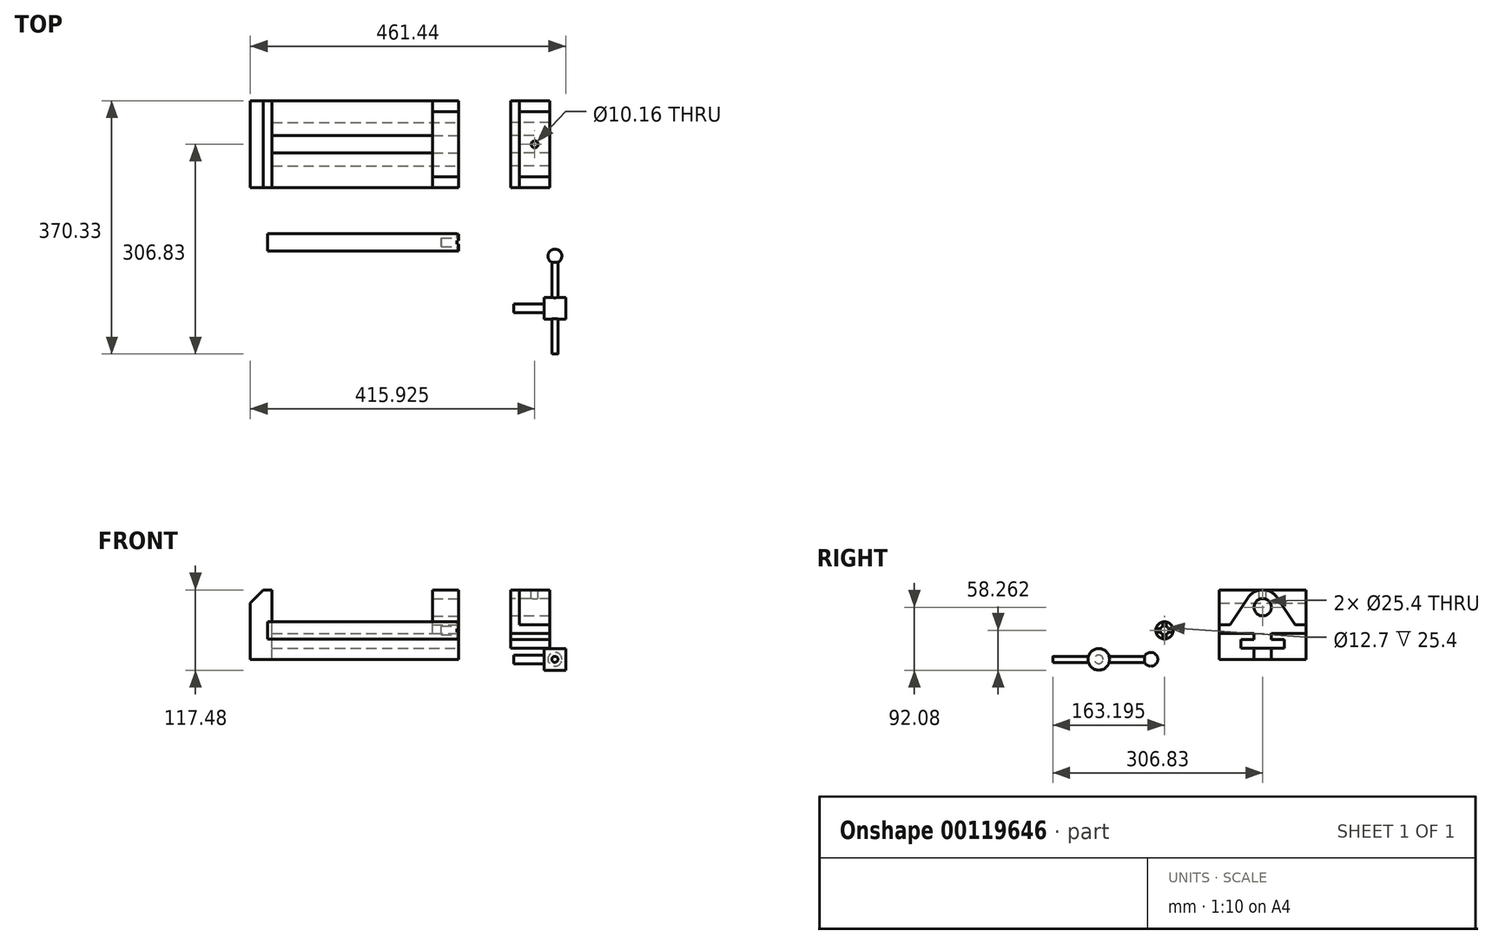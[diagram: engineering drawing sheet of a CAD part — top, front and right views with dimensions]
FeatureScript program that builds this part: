
annotation { "Feature Type Name" : "Feature", "Feature Type Description" : "" }
export const myFeature = defineFeature(function(context is Context, id is Id, definition is map)
    precondition{}
    {
        {
            var Q0;
            Q0=qCreatedBy(makeId("Right.planeOp"),FACE);
            var sketch = newSketch(context, id + "F0", { "sketchPlane" : qUnion([Q0])});
            skLineSegment(sketch, "E0", {"start": v(0, 0) * mm, "end": v(127, 0) * mm});
            skLineSegment(sketch, "E1", {"start": v(127, 0) * mm, "end": v(127, 50.8) * mm});
            skLineSegment(sketch, "E2", {"start": v(127, 50.8) * mm, "end": v(111.12, 50.8) * mm});
            skLineSegment(sketch, "E3", {"start": v(111.12, 50.8) * mm, "end": v(84.6, 90.35) * mm});
            skLineSegment(sketch, "E4", {"start": v(0, 0) * mm, "end": v(0, 50.8) * mm});
            skLineSegment(sketch, "E5", {"start": v(0, 50.8) * mm, "end": v(15.88, 50.8) * mm});
            skLineSegment(sketch, "E6", {"start": v(15.88, 50.8) * mm, "end": v(42.4, 90.35) * mm});
            skLineSegment(sketch, "E7", {"start": v(50.8, 0) * mm, "end": v(50.8, 16.51) * mm});
            skLineSegment(sketch, "E8", {"start": v(50.8, 16.51) * mm, "end": v(31.75, 16.5) * mm});
            skLineSegment(sketch, "E9", {"start": v(31.75, 16.51) * mm, "end": v(31.75, 29.2) * mm});
            skLineSegment(sketch, "E10", {"start": v(31.75, 29.2) * mm, "end": v(50.8, 29.2) * mm});
            skLineSegment(sketch, "E11", {"start": v(50.8, 29.2) * mm, "end": v(50.8, 38.1) * mm});
            skLineSegment(sketch, "E12", {"start": v(50.8, 38.1) * mm, "end": v(76.2, 38.1) * mm});
            skLineSegment(sketch, "E13", {"start": v(76.2, 38.1) * mm, "end": v(76.2, 29.2) * mm});
            skLineSegment(sketch, "E14", {"start": v(76.2, 29.2) * mm, "end": v(95.25, 29.2) * mm});
            skLineSegment(sketch, "E15", {"start": v(95.25, 29.2) * mm, "end": v(95.25, 16.51) * mm});
            skLineSegment(sketch, "E16", {"start": v(95.25, 16.51) * mm, "end": v(76.2, 16.51) * mm});
            skLineSegment(sketch, "E17", {"start": v(76.2, 16.51) * mm, "end": v(76.2, 0) * mm});
            skLineSegment(sketch, "E18", {"start": v(63.5, 0) * mm, "end": v(63.5, 76.2) * mm, "construction": true});
            skCircle(sketch, "E19", {"center": v(63.5, 76.2) * mm, "radius": 12.7 * mm});
            skArc(sketch, "E20", {"start": v(84.6, 90.35) * mm, "mid": v(63.5, 101.6) * mm, "end": v(42.4, 90.35) * mm});
            skLineSegment(sketch, "E21", {"start": v(15.88, 50.8) * mm, "end": v(111.12, 50.8) * mm});
            skLineSegment(sketch, "E22", {"start": v(50.8, 38.1) * mm, "end": v(0, 38.1) * mm});
            skLineSegment(sketch, "E23", {"start": v(76.2, 38.1) * mm, "end": v(127, 38.1) * mm});
            skSolve(sketch);
        }
        {
            var Q0;
            {var subQ0=sQuery(id+"F0.wireOp",EDGE,"E7");Q0=makeQuery(id+"F0.imprint","IMPRINT",FACE,{"disambiguationData":[TD([[makeQuery(id+"F0.imprint","IMPRINT",EDGE,{"derivedFrom":subQ0}),1.0]])]});}
            var Q1;
            Q1=makeQuery(id+"F0.imprint","IMPRINT",FACE,{"disambiguationData":[TD([[makeQuery(id+"F0.imprint","IMPRINT",EDGE,{"derivedFrom":sQuery(id+"F0.wireOp",EDGE,"E13")}),1.0]])]});
            var Q2;
            Q2=makeQuery(id+"F0.imprint","IMPRINT",FACE,{"disambiguationData":[TD([[makeQuery(id+"F0.imprint","IMPRINT",EDGE,{"derivedFrom":sQuery(id+"F0.wireOp",EDGE,"E3")}),1.0]])]});
            var Q3;
            {var subQ3=sQuery(id+"F0.wireOp",EDGE,"E2");Q3=makeQuery(id+"F0.imprint","IMPRINT",FACE,{"disambiguationData":[TD([[makeQuery(id+"F0.imprint","IMPRINT",EDGE,{"derivedFrom":subQ3}),1.0]])]});}
            extrude(context, id + "F1", {"entities" : qUnion([Q0, Q1, Q2, Q3]), "oppositeDirection" : true, "depth" : 38.1 * mm});
        }
        {
            var Q0;
            Q0=makeQuery(id+"F0.imprint","IMPRINT",FACE,{"disambiguationData":[TD([[makeQuery(id+"F0.imprint","IMPRINT",EDGE,{"derivedFrom":sQuery(id+"F0.wireOp",EDGE,"E13")}),1.0]])]});
            var Q1;
            {var subQ0=sQuery(id+"F0.wireOp",EDGE,"E7");Q1=makeQuery(id+"F0.imprint","IMPRINT",FACE,{"disambiguationData":[TD([[makeQuery(id+"F0.imprint","IMPRINT",EDGE,{"derivedFrom":subQ0}),1.0]])]});}
            extrude(context, id + "F2", {"entities" : qUnion([Q0, Q1]), "operationType" : NewBodyOperationType.ADD, "oppositeDirection" : true, "depth" : 304.8 * mm});
        }
        {
            var Q0;
            Q0=makeQuery(id+"F2.opExtrude","CAP_FACE",FACE,{"disambiguationData":[OSD([sQuery(id+"F0.wireOp",EDGE,"E0"),sQuery(id+"F0.wireOp",EDGE,"E4"),sQuery(id+"F0.wireOp",EDGE,"E7"),sQuery(id+"F0.wireOp",EDGE,"E8"),sQuery(id+"F0.wireOp",EDGE,"E9"),sQuery(id+"F0.wireOp",EDGE,"E10"),sQuery(id+"F0.wireOp",EDGE,"E11"),sQuery(id+"F0.wireOp",EDGE,"E22")])],"isStart":false});
            var sketch = newSketch(context, id + "F3", { "sketchPlane" : qUnion([Q0])});
            skLineSegment(sketch, "E24.bottom", {"start": v(0, 0) * mm, "end": v(-127, 0) * mm});
            skLineSegment(sketch, "E24.top", {"start": v(0, 101.6) * mm, "end": v(-127, 101.6) * mm});
            skLineSegment(sketch, "E24.left", {"start": v(0, 0) * mm, "end": v(0, 101.6) * mm});
            skLineSegment(sketch, "E24.right", {"start": v(-127, 0) * mm, "end": v(-127, 101.6) * mm});
            skSolve(sketch);
        }
        {
            var Q0;
            Q0 = qSketchRegion(id + "F3", true);
            extrude(context, id + "F4", {"entities" : qUnion([Q0]), "operationType" : NewBodyOperationType.ADD, "oppositeDirection" : true, "depth" : 31.75 * mm});
        }
        {
            var Q0;
            Q0=makeQuery(id+"F4.opExtrude","CAP_EDGE",EDGE,{"disambiguationData":[OSD([sQuery(id+"F3.wireOp",EDGE,"E24.top")])],"isStart":true});
            chamfer(context, id + "F5", {"entities" : qUnion([Q0]), "chamferType" : ChamferType.TWO_OFFSETS, "width1" : 19.05 * mm, "oppositeDirection" : false, "width2" : 19.05 * mm, "tangentPropagation" : true});
        }
        {
            var Q0;
            {var subQ0=sQuery(id+"F0.wireOp",EDGE,"E7");Q0=makeQuery(id+"F0.imprint","IMPRINT",FACE,{"disambiguationData":[TD([[makeQuery(id+"F0.imprint","IMPRINT",EDGE,{"derivedFrom":subQ0}),1.0]])]});}
            cPlane(context, id + "F6", {"entities" : qUnion([Q0]), "cplaneType" : CPlaneType.OFFSET, "offset" : 76.2 * mm, "width" : 152.4 * mm, "height" : 152.4 * mm});
        }
        {
            var Q0;
            Q0=qCreatedBy(id+"F6.planeOp",FACE);
            var sketch = newSketch(context, id + "F7", { "sketchPlane" : qUnion([Q0])});
            skLineSegment(sketch, "E25.0.0", {"start": v(15.88, 50.8) * mm, "end": v(111.12, 50.8) * mm});
            skLineSegment(sketch, "E25.0.1", {"start": v(111.12, 50.8) * mm, "end": v(84.6, 90.35) * mm});
            skArc(sketch, "E25.0.2", {"start": v(84.6, 90.35) * mm, "mid": v(63.5, 101.6) * mm, "end": v(42.4, 90.35) * mm});
            skLineSegment(sketch, "E25.0.3", {"start": v(42.4, 90.35) * mm, "end": v(15.88, 50.8) * mm});
            skLineSegment(sketch, "E26.0.0", {"start": v(76.2, 38.1) * mm, "end": v(127, 38.1) * mm});
            skLineSegment(sketch, "E26.0.1", {"start": v(127, 38.1) * mm, "end": v(127, 50.8) * mm});
            skLineSegment(sketch, "E26.0.2", {"start": v(127, 50.8) * mm, "end": v(111.12, 50.8) * mm});
            skLineSegment(sketch, "E26.0.3", {"start": v(111.12, 50.8) * mm, "end": v(15.88, 50.8) * mm});
            skLineSegment(sketch, "E26.0.4", {"start": v(15.88, 50.8) * mm, "end": v(0, 50.8) * mm});
            skLineSegment(sketch, "E26.0.5", {"start": v(0, 50.8) * mm, "end": v(0, 38.1) * mm});
            skLineSegment(sketch, "E26.0.6", {"start": v(0, 38.1) * mm, "end": v(50.8, 38.1) * mm});
            skLineSegment(sketch, "E26.0.7", {"start": v(50.8, 38.1) * mm, "end": v(76.2, 38.1) * mm});
            skLineSegment(sketch, "E27.0.0", {"start": v(76.2, 16.51) * mm, "end": v(76.2, 0) * mm});
            skLineSegment(sketch, "E27.0.1", {"start": v(76.2, 0) * mm, "end": v(127, 0) * mm});
            skLineSegment(sketch, "E27.0.2", {"start": v(127, 0) * mm, "end": v(127, 38.1) * mm});
            skLineSegment(sketch, "E27.0.3", {"start": v(127, 38.1) * mm, "end": v(76.2, 38.1) * mm});
            skLineSegment(sketch, "E27.0.4", {"start": v(76.2, 38.1) * mm, "end": v(76.2, 29.2) * mm});
            skLineSegment(sketch, "E27.0.5", {"start": v(76.2, 29.2) * mm, "end": v(95.25, 29.2) * mm});
            skLineSegment(sketch, "E27.0.6", {"start": v(95.25, 29.2) * mm, "end": v(95.25, 16.51) * mm});
            skLineSegment(sketch, "E27.0.7", {"start": v(95.25, 16.51) * mm, "end": v(76.2, 16.51) * mm});
            skLineSegment(sketch, "E28.0.0", {"start": v(0, 38.1) * mm, "end": v(0, 0) * mm});
            skLineSegment(sketch, "E28.0.1", {"start": v(0, 0) * mm, "end": v(50.8, 0) * mm});
            skLineSegment(sketch, "E28.0.2", {"start": v(50.8, 0) * mm, "end": v(50.8, 16.51) * mm});
            skLineSegment(sketch, "E28.0.3", {"start": v(50.8, 16.51) * mm, "end": v(31.75, 16.5) * mm});
            skLineSegment(sketch, "E28.0.4", {"start": v(31.75, 16.51) * mm, "end": v(31.75, 29.2) * mm});
            skLineSegment(sketch, "E28.0.5", {"start": v(31.75, 29.2) * mm, "end": v(50.8, 29.2) * mm});
            skLineSegment(sketch, "E28.0.6", {"start": v(50.8, 29.2) * mm, "end": v(50.8, 38.1) * mm});
            skLineSegment(sketch, "E28.0.7", {"start": v(50.8, 38.1) * mm, "end": v(0, 38.1) * mm});
            skLineSegment(sketch, "E29.0", {"start": v(0, 0) * mm, "end": v(127, 0) * mm});
            skLineSegment(sketch, "E30", {"start": v(76.2, 16.51) * mm, "end": v(50.8, 16.51) * mm});
            skLineSegment(sketch, "E31.0.0", {"start": v(50.8, 16.51) * mm, "end": v(50.8, 0) * mm});
            skLineSegment(sketch, "E31.0.1", {"start": v(50.8, 0) * mm, "end": v(76.2, 0) * mm});
            skLineSegment(sketch, "E31.0.2", {"start": v(76.2, 0) * mm, "end": v(76.2, 16.51) * mm});
            skLineSegment(sketch, "E31.0.3", {"start": v(76.2, 16.51) * mm, "end": v(95.25, 16.51) * mm});
            skLineSegment(sketch, "E31.0.4", {"start": v(95.25, 16.51) * mm, "end": v(95.25, 29.2) * mm});
            skLineSegment(sketch, "E31.0.5", {"start": v(95.25, 29.2) * mm, "end": v(76.2, 29.2) * mm});
            skLineSegment(sketch, "E31.0.6", {"start": v(76.2, 29.2) * mm, "end": v(76.2, 38.1) * mm});
            skLineSegment(sketch, "E31.0.8", {"start": v(127, 38.1) * mm, "end": v(127, 101.6) * mm});
            skLineSegment(sketch, "E31.0.9", {"start": v(127, 101.6) * mm, "end": v(0, 101.6) * mm});
            skLineSegment(sketch, "E31.0.10", {"start": v(0, 101.6) * mm, "end": v(0, 38.1) * mm});
            skLineSegment(sketch, "E31.0.12", {"start": v(50.8, 38.1) * mm, "end": v(50.8, 29.2) * mm});
            skLineSegment(sketch, "E31.0.13", {"start": v(50.8, 29.2) * mm, "end": v(31.75, 29.2) * mm});
            skLineSegment(sketch, "E31.0.14", {"start": v(31.75, 29.2) * mm, "end": v(31.75, 16.51) * mm});
            skLineSegment(sketch, "E31.0.15", {"start": v(31.75, 16.5) * mm, "end": v(50.8, 16.51) * mm});
            skCircle(sketch, "E32.0", {"center": v(63.5, 76.2) * mm, "radius": 12.7 * mm});
            skSolve(sketch);
        }
        {
            var Q0;
            {var subQ2=sQuery(id+"F7.wireOp",EDGE,"E26.0.2");Q0=makeQuery(id+"F7.imprint","IMPRINT",FACE,{"disambiguationData":[TD([[makeQuery(id+"F7.imprint","IMPRINT",EDGE,{"derivedFrom":subQ2}),1.0]])]});}
            var Q1;
            {var subQ3=sQuery(id+"F7.wireOp",EDGE,"E25.0.1");Q1=makeQuery(id+"F7.imprint","IMPRINT",FACE,{"disambiguationData":[TD([[makeQuery(id+"F7.imprint","IMPRINT",EDGE,{"derivedFrom":subQ3}),1.0]])]});}
            var Q2;
            Q2=makeQuery(id+"F7.imprint","IMPRINT",FACE,{"disambiguationData":[TD([[makeQuery(id+"F7.imprint","IMPRINT",EDGE,{"derivedFrom":sQuery(id+"F7.wireOp",EDGE,"E26.0.7")}),-1.0]])]});
            extrude(context, id + "F8", {"entities" : qUnion([Q0, Q1, Q2]), "depth" : 57.15 * mm});
        }
        {
            var Q0;
            {var subQ5=sQuery(id+"F7.wireOp",EDGE,"E25.0.3");Q0=makeQuery(id+"F7.imprint","IMPRINT",FACE,{"disambiguationData":[TD([[makeQuery(id+"F7.imprint","IMPRINT",EDGE,{"derivedFrom":subQ5}),-1.0]])]});}
            var Q1;
            {var subQ5=sQuery(id+"F7.wireOp",EDGE,"E25.0.1");Q1=makeQuery(id+"F7.imprint","IMPRINT",FACE,{"disambiguationData":[TD([[makeQuery(id+"F7.imprint","IMPRINT",EDGE,{"derivedFrom":subQ5}),-1.0]])]});}
            extrude(context, id + "F9", {"entities" : qUnion([Q0, Q1]), "operationType" : NewBodyOperationType.ADD, "depth" : 12.7 * mm});
        }
        {
            var Q0;
            {var subQ0=sQuery(id+"F7.wireOp",EDGE,"E31.0.9");Q0=makeQuery(id+"F9.boolean.opBoolean","MERGE",FACE,{"derivedFrom":[makeQuery(id+"F9.opExtrude","SWEPT_FACE",FACE,{"disambiguationData":[OSD([subQ0]),TDD([makeQuery(id+"F7.imprint","IMPRINT",EDGE,{"disambiguationData":[TD([[makeQuery(id+"F7.imprint","INTERSECT",VERTEX,{"derivedFrom":[sQuery(id+"F7.wireOp",EDGE,"E31.0.8"),subQ0]}),-1.0]])],"derivedFrom":subQ0})])]}),makeQuery(id+"F9.opExtrude","SWEPT_FACE",FACE,{"disambiguationData":[OSD([subQ0]),TDD([makeQuery(id+"F7.imprint","IMPRINT",EDGE,{"disambiguationData":[TD([[makeQuery(id+"F7.imprint","INTERSECT",VERTEX,{"derivedFrom":[subQ0,sQuery(id+"F7.wireOp",EDGE,"E31.0.10")]}),1.0]])],"derivedFrom":subQ0})])]})]});}
            var sketch = newSketch(context, id + "F10", { "sketchPlane" : qUnion([Q0])});
            skCircle(sketch, "E33", {"center": v(111.13, 63.5) * mm, "radius": 5.08 * mm});
            skSolve(sketch);
        }
        {
            var Q0;
            Q0=makeQuery(id+"F10.imprint","IMPRINT",FACE,{"disambiguationData":[TD([[makeQuery(id+"F10.imprint","IMPRINT",EDGE,{"derivedFrom":sQuery(id+"F10.wireOp",EDGE,"E33")}),1.0]])]});
            var Q1;
            Q1=makeQuery(id+"F8.opExtrude","SWEPT_FACE",FACE,{"disambiguationData":[OSD([sQuery(id+"F7.wireOp",EDGE,"E32.0")])]});
            extrude(context, id + "F11", {"entities" : qUnion([Q0]), "operationType" : NewBodyOperationType.REMOVE, "endBound" : BoundingType.UP_TO_SURFACE, "oppositeDirection" : true, "endBoundEntityFace" : qUnion([Q1]), "depth" : 25.4 * mm});
        }
        {
            var Q0;
            Q0=qCreatedBy(makeId("Right.planeOp"),FACE);
            var sketch = newSketch(context, id + "F12", { "sketchPlane" : qUnion([Q0])});
            skCircle(sketch, "E34", {"center": v(-80.14, 42.38) * mm, "radius": 6.35 * mm});
            skCircle(sketch, "E35", {"center": v(-80.14, 42.38) * mm, "radius": 12.7 * mm});
            skLineSegment(sketch, "E36", {"start": v(-80.14, 42.38) * mm, "end": v(0, 0) * mm, "construction": true});
            skLineSegment(sketch, "E37", {"start": v(-82.68, 36.56) * mm, "end": v(-82.68, 29.94) * mm});
            skLineSegment(sketch, "E38", {"start": v(-77.6, 36.56) * mm, "end": v(-77.6, 29.94) * mm});
            skLineSegment(sketch, "E39", {"start": v(-82.68, 48.2) * mm, "end": v(-82.68, 54.83) * mm});
            skLineSegment(sketch, "E40", {"start": v(-77.6, 48.2) * mm, "end": v(-77.6, 54.83) * mm});
            skLineSegment(sketch, "E41", {"start": v(-74.32, 44.92) * mm, "end": v(-67.7, 44.92) * mm});
            skLineSegment(sketch, "E42", {"start": v(-74.32, 39.84) * mm, "end": v(-67.7, 39.84) * mm});
            skLineSegment(sketch, "E43", {"start": v(-85.96, 44.92) * mm, "end": v(-92.58, 44.92) * mm});
            skLineSegment(sketch, "E44", {"start": v(-85.96, 39.84) * mm, "end": v(-92.58, 39.84) * mm});
            skSolve(sketch);
        }
        {
            var Q0;
            Q0 = qSketchRegion(id + "F12", true);
            var Q1;
            {var subQ0=sQuery(id+"F12.wireOp",EDGE,"E34");var subQ6=makeQuery(id+"F12.imprint","INTERSECT",VERTEX,{"derivedFrom":[subQ0,sQuery(id+"F12.wireOp",EDGE,"E40")]});Q1=makeQuery(id+"F12.imprint","IMPRINT",FACE,{"disambiguationData":[TD([[makeQuery(id+"F12.imprint","IMPRINT",EDGE,{"disambiguationData":[TD([[subQ6,1.0]])],"derivedFrom":subQ0}),1.0]])]});}
            extrude(context, id + "F13", {"entities" : qUnion([Q0, Q1]), "oppositeDirection" : true, "depth" : 279.4 * mm});
        }
        {
            var Q0;
            {var subQ0=sQuery(id+"F12.wireOp",EDGE,"E34");var subQ6=makeQuery(id+"F12.imprint","INTERSECT",VERTEX,{"derivedFrom":[subQ0,sQuery(id+"F12.wireOp",EDGE,"E40")]});Q0=makeQuery(id+"F12.imprint","IMPRINT",FACE,{"disambiguationData":[TD([[makeQuery(id+"F12.imprint","IMPRINT",EDGE,{"disambiguationData":[TD([[subQ6,1.0]])],"derivedFrom":subQ0}),1.0]])]});}
            extrude(context, id + "F14", {"entities" : qUnion([Q0]), "operationType" : NewBodyOperationType.REMOVE, "oppositeDirection" : true, "depth" : 25.4 * mm});
        }
        {
            var Q0;
            {var subQ0=sQuery(id+"F12.wireOp",EDGE,"E39");Q0=makeQuery(id+"F12.imprint","IMPRINT",FACE,{"disambiguationData":[TD([[makeQuery(id+"F12.imprint","IMPRINT",EDGE,{"derivedFrom":subQ0}),-1.0]])]});}
            var Q1;
            {var subQ0=sQuery(id+"F12.wireOp",EDGE,"E41");Q1=makeQuery(id+"F12.imprint","IMPRINT",FACE,{"disambiguationData":[TD([[makeQuery(id+"F12.imprint","IMPRINT",EDGE,{"derivedFrom":subQ0}),-1.0]])]});}
            var Q2;
            {var subQ0=sQuery(id+"F12.wireOp",EDGE,"E37");Q2=makeQuery(id+"F12.imprint","IMPRINT",FACE,{"disambiguationData":[TD([[makeQuery(id+"F12.imprint","IMPRINT",EDGE,{"derivedFrom":subQ0}),1.0]])]});}
            var Q3;
            {var subQ0=sQuery(id+"F12.wireOp",EDGE,"E43");Q3=makeQuery(id+"F12.imprint","IMPRINT",FACE,{"disambiguationData":[TD([[makeQuery(id+"F12.imprint","IMPRINT",EDGE,{"derivedFrom":subQ0}),1.0]])]});}
            extrude(context, id + "F15", {"entities" : qUnion([Q0, Q1, Q2, Q3]), "operationType" : NewBodyOperationType.REMOVE, "oppositeDirection" : true, "depth" : 2.54 * mm});
        }
        {
            var Q0;
            Q0=qCreatedBy(makeId("Top.planeOp"),FACE);
            var sketch = newSketch(context, id + "F16", { "sketchPlane" : qUnion([Q0])});
            skLineSegment(sketch, "E45", {"start": v(0, 0) * mm, "end": v(140.77, -176.27) * mm, "construction": true});
            skLineSegment(sketch, "E46", {"start": v(140.77, -176.27) * mm, "end": v(140.77, -100.07) * mm, "construction": true});
            skLineSegment(sketch, "E47", {"start": v(171.85, -176.27) * mm, "end": v(140.77, -176.27) * mm, "construction": true});
            skLineSegment(sketch, "E48", {"start": v(54.06, -176.27) * mm, "end": v(140.77, -176.27) * mm, "construction": true});
            skLineSegment(sketch, "E49", {"start": v(145.21, -100.07) * mm, "end": v(145.21, -176.27) * mm});
            skLineSegment(sketch, "E50", {"start": v(136.32, -100.07) * mm, "end": v(136.32, -176.27) * mm});
            skLineSegment(sketch, "E51", {"start": v(145.21, -100.07) * mm, "end": v(136.32, -100.07) * mm});
            skCircle(sketch, "E52", {"center": v(140.77, -100.07) * mm, "radius": 10.16 * mm});
            skLineSegment(sketch, "E53", {"start": v(156.64, -160.4) * mm, "end": v(124.9, -160.4) * mm});
            skLineSegment(sketch, "E54", {"start": v(156.64, -160.4) * mm, "end": v(156.64, -176.27) * mm});
            skLineSegment(sketch, "E55", {"start": v(124.9, -160.4) * mm, "end": v(124.9, -176.27) * mm});
            skLineSegment(sketch, "E56", {"start": v(124.9, -169.92) * mm, "end": v(80.44, -169.92) * mm});
            skLineSegment(sketch, "E57", {"start": v(80.44, -169.92) * mm, "end": v(80.44, -176.27) * mm});
            skLineSegment(sketch, "E58.MirrorCS", {"start": v(156.64, -192.14) * mm, "end": v(156.64, -176.27) * mm});
            skLineSegment(sketch, "E59.MirrorCS", {"start": v(156.64, -192.14) * mm, "end": v(124.9, -192.14) * mm});
            skLineSegment(sketch, "E60.MirrorCS", {"start": v(124.9, -192.14) * mm, "end": v(124.9, -176.27) * mm});
            skLineSegment(sketch, "E61.MirrorCS", {"start": v(124.9, -182.62) * mm, "end": v(80.44, -182.62) * mm});
            skLineSegment(sketch, "E62.MirrorCS", {"start": v(80.44, -182.62) * mm, "end": v(80.44, -176.27) * mm});
            skCircle(sketch, "E63.MirrorC", {"center": v(140.77, -252.47) * mm, "radius": 10.16 * mm});
            skLineSegment(sketch, "E64.MirrorCS", {"start": v(145.21, -252.47) * mm, "end": v(145.21, -176.27) * mm});
            skLineSegment(sketch, "E65.MirrorCS", {"start": v(136.32, -252.47) * mm, "end": v(136.32, -176.27) * mm});
            skLineSegment(sketch, "E66.MirrorCS", {"start": v(145.21, -252.47) * mm, "end": v(136.32, -252.47) * mm});
            skLineSegment(sketch, "E67", {"start": v(140.77, -89.9) * mm, "end": v(140.77, -262.63) * mm});
            skLineSegment(sketch, "E68", {"start": v(156.64, -176.27) * mm, "end": v(80.44, -176.27) * mm});
            skSolve(sketch);
        }
        {
            var Q0;
            {var subQ0=sQuery(id+"F16.wireOp",EDGE,"E51");var subQ1=sQuery(id+"F16.wireOp",EDGE,"E49");var subQ2=makeQuery(id+"F16.imprint","INTERSECT",VERTEX,{"derivedFrom":[subQ1,subQ0]});Q0=makeQuery(id+"F16.imprint","IMPRINT",FACE,{"disambiguationData":[TD([[makeQuery(id+"F16.imprint","IMPRINT",EDGE,{"disambiguationData":[TD([[subQ2,-1.0]])],"derivedFrom":subQ1}),1.0]])]});}
            var Q1;
            {var subQ0=sQuery(id+"F16.wireOp",EDGE,"E51");var subQ1=sQuery(id+"F16.wireOp",EDGE,"E49");var subQ2=makeQuery(id+"F16.imprint","INTERSECT",VERTEX,{"derivedFrom":[subQ1,subQ0]});Q1=makeQuery(id+"F16.imprint","IMPRINT",FACE,{"disambiguationData":[TD([[makeQuery(id+"F16.imprint","IMPRINT",EDGE,{"disambiguationData":[TD([[subQ2,-1.0]])],"derivedFrom":subQ1}),-1.0]])]});}
            var Q2;
            {var subQ0=sQuery(id+"F16.wireOp",EDGE,"E52");var subQ1=sQuery(id+"F16.wireOp",EDGE,"E49");var subQ2=makeQuery(id+"F16.imprint","INTERSECT",VERTEX,{"derivedFrom":[subQ1,subQ0]});Q2=makeQuery(id+"F16.imprint","IMPRINT",FACE,{"disambiguationData":[TD([[makeQuery(id+"F16.imprint","IMPRINT",EDGE,{"disambiguationData":[TD([[subQ2,-1.0]])],"derivedFrom":subQ1}),-1.0]])]});}
            var Q3;
            {var subQ1=sQuery(id+"F16.wireOp",EDGE,"E49");var subQ3=sQuery(id+"F16.wireOp",EDGE,"E53");var subQ4=makeQuery(id+"F16.imprint","INTERSECT",VERTEX,{"derivedFrom":[subQ1,subQ3]});Q3=makeQuery(id+"F16.imprint","IMPRINT",FACE,{"disambiguationData":[TD([[makeQuery(id+"F16.imprint","IMPRINT",EDGE,{"disambiguationData":[TD([[subQ4,-1.0]])],"derivedFrom":subQ3}),1.0]])]});}
            var Q4;
            {var subQ0=sQuery(id+"F16.wireOp",EDGE,"E64.MirrorCS");var subQ1=sQuery(id+"F16.wireOp",EDGE,"E59.MirrorCS");var subQ2=makeQuery(id+"F16.imprint","INTERSECT",VERTEX,{"derivedFrom":[subQ1,subQ0]});Q4=makeQuery(id+"F16.imprint","IMPRINT",FACE,{"disambiguationData":[TD([[makeQuery(id+"F16.imprint","IMPRINT",EDGE,{"disambiguationData":[TD([[subQ2,-1.0]])],"derivedFrom":subQ1}),-1.0]])]});}
            var Q5;
            {var subQ0=sQuery(id+"F16.wireOp",EDGE,"E64.MirrorCS");var subQ1=sQuery(id+"F16.wireOp",EDGE,"E59.MirrorCS");var subQ2=makeQuery(id+"F16.imprint","INTERSECT",VERTEX,{"derivedFrom":[subQ1,subQ0]});Q5=makeQuery(id+"F16.imprint","IMPRINT",FACE,{"disambiguationData":[TD([[makeQuery(id+"F16.imprint","IMPRINT",EDGE,{"disambiguationData":[TD([[subQ2,-1.0]])],"derivedFrom":subQ1}),1.0]])]});}
            var Q6;
            {var subQ0=sQuery(id+"F16.wireOp",EDGE,"E64.MirrorCS");var subQ1=sQuery(id+"F16.wireOp",EDGE,"E63.MirrorC");var subQ2=makeQuery(id+"F16.imprint","INTERSECT",VERTEX,{"derivedFrom":[subQ1,subQ0]});Q6=makeQuery(id+"F16.imprint","IMPRINT",FACE,{"disambiguationData":[TD([[makeQuery(id+"F16.imprint","IMPRINT",EDGE,{"disambiguationData":[TD([[subQ2,1.0]])],"derivedFrom":subQ1}),-1.0]])]});}
            var Q7;
            {var subQ0=sQuery(id+"F16.wireOp",EDGE,"E67");var subQ1=sQuery(id+"F16.wireOp",EDGE,"E63.MirrorC");var subQ2=makeQuery(id+"F16.imprint","INTERSECT",VERTEX,{"disambiguationData":[OD(0.0)],"derivedFrom":[subQ1,subQ0]});Q7=makeQuery(id+"F16.imprint","IMPRINT",FACE,{"disambiguationData":[TD([[makeQuery(id+"F16.imprint","IMPRINT",EDGE,{"disambiguationData":[TD([[subQ2,1.0]])],"derivedFrom":subQ1}),-1.0]])]});}
            var Q8;
            Q8=sQuery(id+"F16.wireOp",EDGE,"E67");
            revolve(context, id + "F17", {"entities" : qUnion([Q0, Q1, Q2, Q3, Q4, Q5, Q6, Q7]), "axis" : qUnion([Q8]), "revolveType" : RevolveType.FULL});
        }
        {
            var Q0;
            {var subQ5=sQuery(id+"F16.wireOp",EDGE,"E54");Q0=makeQuery(id+"F16.imprint","IMPRINT",FACE,{"disambiguationData":[TD([[makeQuery(id+"F16.imprint","IMPRINT",EDGE,{"derivedFrom":subQ5}),-1.0]])]});}
            var Q1;
            {var subQ1=sQuery(id+"F16.wireOp",EDGE,"E55");var subQ4=sQuery(id+"F16.wireOp",EDGE,"E53");var subQ5=makeQuery(id+"F16.imprint","INTERSECT",VERTEX,{"derivedFrom":[subQ4,subQ1]});Q1=makeQuery(id+"F16.imprint","IMPRINT",FACE,{"disambiguationData":[TD([[makeQuery(id+"F16.imprint","IMPRINT",EDGE,{"disambiguationData":[TD([[subQ5,1.0]])],"derivedFrom":subQ4}),1.0]])]});}
            var Q2;
            {var subQ3=sQuery(id+"F16.wireOp",EDGE,"E56");Q2=makeQuery(id+"F16.imprint","IMPRINT",FACE,{"disambiguationData":[TD([[makeQuery(id+"F16.imprint","IMPRINT",EDGE,{"derivedFrom":subQ3}),1.0]])]});}
            var Q3;
            {var subQ1=sQuery(id+"F16.wireOp",EDGE,"E49");var subQ3=sQuery(id+"F16.wireOp",EDGE,"E53");var subQ4=makeQuery(id+"F16.imprint","INTERSECT",VERTEX,{"derivedFrom":[subQ1,subQ3]});Q3=makeQuery(id+"F16.imprint","IMPRINT",FACE,{"disambiguationData":[TD([[makeQuery(id+"F16.imprint","IMPRINT",EDGE,{"disambiguationData":[TD([[subQ4,-1.0]])],"derivedFrom":subQ3}),1.0]])]});}
            var Q4;
            {var subQ1=sQuery(id+"F16.wireOp",EDGE,"E50");var subQ3=sQuery(id+"F16.wireOp",EDGE,"E53");var subQ4=makeQuery(id+"F16.imprint","INTERSECT",VERTEX,{"derivedFrom":[subQ1,subQ3]});Q4=makeQuery(id+"F16.imprint","IMPRINT",FACE,{"disambiguationData":[TD([[makeQuery(id+"F16.imprint","IMPRINT",EDGE,{"disambiguationData":[TD([[subQ4,1.0]])],"derivedFrom":subQ3}),1.0]])]});}
            var Q5;
            Q5=sQuery(id+"F16.wireOp",EDGE,"E68");
            revolve(context, id + "F18", {"operationType" : NewBodyOperationType.ADD, "entities" : qUnion([Q0, Q1, Q2, Q3, Q4]), "axis" : qUnion([Q5]), "revolveType" : RevolveType.FULL});
        }
    });
